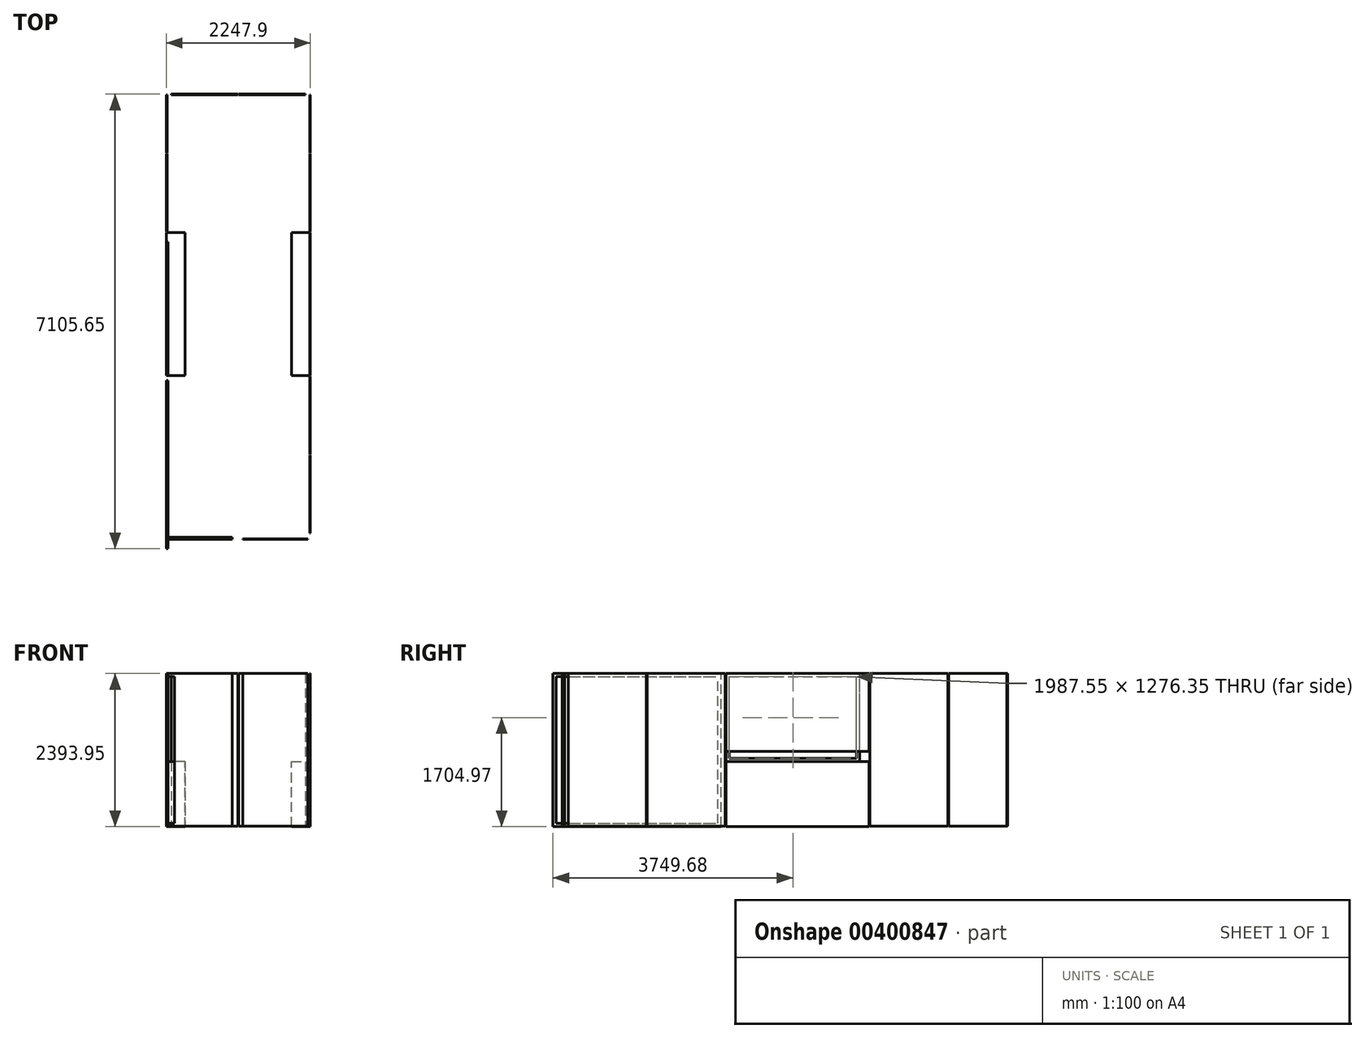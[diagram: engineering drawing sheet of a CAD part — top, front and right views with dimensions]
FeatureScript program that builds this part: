
annotation { "Feature Type Name" : "Feature", "Feature Type Description" : "" }
export const myFeature = defineFeature(function(context is Context, id is Id, definition is map)
    precondition{}
    {
        {
            var Q0;
            Q0=qCreatedBy(makeId("Top.planeOp"),FACE);
            var sketch = newSketch(context, id + "F0", { "sketchPlane" : qUnion([Q0])});
            skLineSegment(sketch, "E0.bottom", {"start": v(0, -6959.6) * mm, "end": v(2247.9, -6959.6) * mm});
            skLineSegment(sketch, "E0.top", {"start": v(0, 0) * mm, "end": v(2247.9, 0) * mm});
            skLineSegment(sketch, "E0.left", {"start": v(0, -6959.6) * mm, "end": v(0, 0) * mm});
            skLineSegment(sketch, "E0.right", {"start": v(2247.9, -6959.6) * mm, "end": v(2247.9, 0) * mm});
            skSolve(sketch);
        }
        {
            var Q0;
            Q0=qSketchRegion(id+"F0",true);
            extrude(context, id + "F1", {"entities" : qUnion([Q0]), "depth" : 2565.4 * mm});
        }
        {
            var Q0;
            Q0=makeQuery(id+"F1.opExtrude","SWEPT_FACE",FACE,{"disambiguationData":[OSD([sQuery(id+"F0.wireOp",EDGE,"E0.left")])]});
            cPlane(context, id + "F2", {"entities" : qUnion([Q0]), "cplaneType" : CPlaneType.OFFSET, "offset" : 0 * mm, "width" : 152.4 * mm, "height" : 152.4 * mm});
        }
        {
            var Q0;
            Q0=makeQuery(id+"F1.opExtrude","SWEPT_FACE",FACE,{"disambiguationData":[OSD([sQuery(id+"F0.wireOp",EDGE,"E0.right")])]});
            cPlane(context, id + "F3", {"entities" : qUnion([Q0]), "cplaneType" : CPlaneType.OFFSET, "offset" : 0 * mm, "width" : 152.4 * mm, "height" : 152.4 * mm});
        }
        {
            var Q0;
            Q0=makeQuery(id+"F1.opExtrude","SWEPT_FACE",FACE,{"disambiguationData":[OSD([sQuery(id+"F0.wireOp",EDGE,"E0.top")])]});
            cPlane(context, id + "F4", {"entities" : qUnion([Q0]), "cplaneType" : CPlaneType.OFFSET, "offset" : 0 * mm, "width" : 152.4 * mm, "height" : 152.4 * mm});
        }
        {
            var Q0;
            Q0=makeQuery(id+"F1.opExtrude","SWEPT_FACE",FACE,{"disambiguationData":[OSD([sQuery(id+"F0.wireOp",EDGE,"E0.bottom")])]});
            cPlane(context, id + "F5", {"entities" : qUnion([Q0]), "cplaneType" : CPlaneType.OFFSET, "offset" : 0 * mm, "width" : 152.4 * mm, "height" : 152.4 * mm});
        }
        {
            var Q0;
            Q0=qCreatedBy(id+"F3.planeOp",FACE);
            var sketch = newSketch(context, id + "F6", { "sketchPlane" : qUnion([Q0])});
            skLineSegment(sketch, "E1.bottom", {"start": v(-5632.45, 6.35) * mm, "end": v(-4413.25, 6.35) * mm});
            skLineSegment(sketch, "E1.top", {"start": v(-5632.45, 2393.95) * mm, "end": v(-4413.25, 2393.95) * mm});
            skLineSegment(sketch, "E1.left", {"start": v(-5632.45, 6.35) * mm, "end": v(-5632.45, 2393.95) * mm});
            skLineSegment(sketch, "E1.right", {"start": v(-4413.25, 6.35) * mm, "end": v(-4413.25, 2393.95) * mm});
            skLineSegment(sketch, "E2.bottom", {"start": v(-4400.55, 2393.95) * mm, "end": v(-2165.35, 2393.95) * mm});
            skLineSegment(sketch, "E2.top", {"start": v(-4400.55, 1174.75) * mm, "end": v(-2165.35, 1174.75) * mm});
            skLineSegment(sketch, "E2.left", {"start": v(-4400.55, 2393.95) * mm, "end": v(-4400.55, 1174.75) * mm});
            skLineSegment(sketch, "E2.right", {"start": v(-2165.35, 2393.95) * mm, "end": v(-2165.35, 1174.75) * mm});
            skLineSegment(sketch, "E3.bottom", {"start": v(-2152.65, 2393.95) * mm, "end": v(-933.45, 2393.95) * mm});
            skLineSegment(sketch, "E3.top", {"start": v(-2152.65, 6.35) * mm, "end": v(-933.45, 6.35) * mm});
            skLineSegment(sketch, "E3.left", {"start": v(-2152.65, 2393.95) * mm, "end": v(-2152.65, 6.35) * mm});
            skLineSegment(sketch, "E3.right", {"start": v(-933.45, 2393.95) * mm, "end": v(-933.45, 6.35) * mm});
            skLineSegment(sketch, "E4.bottom", {"start": v(-6864.35, 6.35) * mm, "end": v(-5645.15, 6.35) * mm});
            skLineSegment(sketch, "E4.top", {"start": v(-6864.35, 2393.95) * mm, "end": v(-5645.15, 2393.95) * mm});
            skLineSegment(sketch, "E4.left", {"start": v(-6864.35, 6.35) * mm, "end": v(-6864.35, 2393.95) * mm});
            skLineSegment(sketch, "E4.right", {"start": v(-5645.15, 6.35) * mm, "end": v(-5645.15, 2393.95) * mm});
            skLineSegment(sketch, "E5.bottom", {"start": v(-2165.35, 0) * mm, "end": v(-4400.55, 0) * mm});
            skLineSegment(sketch, "E5.top", {"start": v(-2165.35, 1016) * mm, "end": v(-4400.55, 1016) * mm});
            skLineSegment(sketch, "E5.left", {"start": v(-2165.35, 0) * mm, "end": v(-2165.35, 1016) * mm});
            skLineSegment(sketch, "E5.right", {"start": v(-4400.55, 0) * mm, "end": v(-4400.55, 1016) * mm});
            skLineSegment(sketch, "E6.bottom", {"start": v(-920.75, 2393.95) * mm, "end": v(-12.7, 2393.95) * mm});
            skLineSegment(sketch, "E6.top", {"start": v(-920.75, 6.35) * mm, "end": v(-12.7, 6.35) * mm});
            skLineSegment(sketch, "E6.left", {"start": v(-920.75, 2393.95) * mm, "end": v(-920.75, 6.35) * mm});
            skLineSegment(sketch, "E6.right", {"start": v(-12.7, 2393.95) * mm, "end": v(-12.7, 6.35) * mm});
            skSolve(sketch);
        }
        {
            var Q0;
            Q0=makeQuery(id+"F6.imprint","IMPRINT",FACE,{"disambiguationData":[TD([[makeQuery(id+"F6.imprint","IMPRINT",EDGE,{"derivedFrom":sQuery(id+"F6.wireOp",EDGE,"E1.bottom")}),1.0]])]});
            var Q1;
            Q1=makeQuery(id+"F6.imprint","IMPRINT",FACE,{"disambiguationData":[TD([[makeQuery(id+"F6.imprint","IMPRINT",EDGE,{"derivedFrom":sQuery(id+"F6.wireOp",EDGE,"E2.bottom")}),-1.0]])]});
            var Q2;
            Q2=makeQuery(id+"F6.imprint","IMPRINT",FACE,{"disambiguationData":[TD([[makeQuery(id+"F6.imprint","IMPRINT",EDGE,{"derivedFrom":sQuery(id+"F6.wireOp",EDGE,"E3.bottom")}),-1.0]])]});
            var Q3;
            Q3=makeQuery(id+"F6.imprint","IMPRINT",FACE,{"disambiguationData":[TD([[makeQuery(id+"F6.imprint","IMPRINT",EDGE,{"derivedFrom":sQuery(id+"F6.wireOp",EDGE,"E4.bottom")}),1.0]])]});
            var Q4;
            Q4=makeQuery(id+"F6.imprint","IMPRINT",FACE,{"disambiguationData":[TD([[makeQuery(id+"F6.imprint","IMPRINT",EDGE,{"derivedFrom":sQuery(id+"F6.wireOp",EDGE,"E6.bottom")}),-1.0]])]});
            extrude(context, id + "F7", {"entities" : qUnion([Q0, Q1, Q2, Q3, Q4]), "oppositeDirection" : true, "depth" : 9.52 * mm});
        }
        {
            var Q0;
            Q0=qCreatedBy(id+"F2.planeOp",FACE);
            var sketch = newSketch(context, id + "F8", { "sketchPlane" : qUnion([Q0])});
            skLineSegment(sketch, "E7.bottom", {"start": v(7105.65, 0) * mm, "end": v(4476.75, 0) * mm});
            skLineSegment(sketch, "E7.top", {"start": v(7105.65, 2393.95) * mm, "end": v(4476.75, 2393.95) * mm});
            skLineSegment(sketch, "E7.left", {"start": v(7105.65, 0) * mm, "end": v(7105.65, 2393.95) * mm});
            skLineSegment(sketch, "E7.right", {"start": v(4476.75, 0) * mm, "end": v(4476.75, 2393.95) * mm});
            skLineSegment(sketch, "E8.bottom", {"start": v(2152.65, 2393.95) * mm, "end": v(933.45, 2393.95) * mm});
            skLineSegment(sketch, "E8.top", {"start": v(2152.65, 6.35) * mm, "end": v(933.45, 6.35) * mm});
            skLineSegment(sketch, "E8.left", {"start": v(2152.65, 2393.95) * mm, "end": v(2152.65, 6.35) * mm});
            skLineSegment(sketch, "E8.right", {"start": v(933.45, 2393.95) * mm, "end": v(933.45, 6.35) * mm});
            skLineSegment(sketch, "E9.bottom", {"start": v(4400.55, 1016) * mm, "end": v(2311.4, 1016) * mm});
            skLineSegment(sketch, "E9.top", {"start": v(4400.55, 2393.95) * mm, "end": v(2311.4, 2393.95) * mm});
            skLineSegment(sketch, "E9.left", {"start": v(4400.55, 1016) * mm, "end": v(4400.55, 2393.95) * mm});
            skLineSegment(sketch, "E9.right", {"start": v(2311.4, 1016) * mm, "end": v(2311.4, 2393.95) * mm});
            skLineSegment(sketch, "E10.0.0", {"start": v(2165.35, 0) * mm, "end": v(2165.35, 1016) * mm});
            skLineSegment(sketch, "E10.0.1", {"start": v(2165.35, 1016) * mm, "end": v(4400.55, 1016) * mm});
            skLineSegment(sketch, "E10.0.2", {"start": v(4400.55, 1016) * mm, "end": v(4400.55, 0) * mm});
            skLineSegment(sketch, "E10.0.3", {"start": v(4400.55, 0) * mm, "end": v(2165.35, 0) * mm});
            skLineSegment(sketch, "E11.bottom", {"start": v(920.75, 2393.95) * mm, "end": v(12.7, 2393.95) * mm});
            skLineSegment(sketch, "E11.top", {"start": v(920.75, 6.35) * mm, "end": v(12.7, 6.35) * mm});
            skLineSegment(sketch, "E11.left", {"start": v(920.75, 2393.95) * mm, "end": v(920.75, 6.35) * mm});
            skLineSegment(sketch, "E11.right", {"start": v(12.7, 2393.95) * mm, "end": v(12.7, 6.35) * mm});
            skSolve(sketch);
        }
        {
            var Q0;
            Q0=qCreatedBy(id+"F4.planeOp",FACE);
            var sketch = newSketch(context, id + "F9", { "sketchPlane" : qUnion([Q0])});
            skLineSegment(sketch, "E12.bottom", {"start": v(-1117.6, 2393.95) * mm, "end": v(-76.2, 2393.95) * mm});
            skLineSegment(sketch, "E12.top", {"start": v(-1117.6, 6.35) * mm, "end": v(-76.2, 6.35) * mm});
            skLineSegment(sketch, "E12.left", {"start": v(-1117.6, 2393.95) * mm, "end": v(-1117.6, 6.35) * mm});
            skLineSegment(sketch, "E12.right", {"start": v(-76.2, 2393.95) * mm, "end": v(-76.2, 6.35) * mm});
            skLineSegment(sketch, "E13.bottom", {"start": v(-1130.3, 2393.95) * mm, "end": v(-2171.7, 2393.95) * mm});
            skLineSegment(sketch, "E13.top", {"start": v(-1130.3, 6.35) * mm, "end": v(-2171.7, 6.35) * mm});
            skLineSegment(sketch, "E13.left", {"start": v(-1130.3, 2393.95) * mm, "end": v(-1130.3, 6.35) * mm});
            skLineSegment(sketch, "E13.right", {"start": v(-2171.7, 2393.95) * mm, "end": v(-2171.7, 6.35) * mm});
            skSolve(sketch);
        }
        {
            var Q0;
            Q0=makeQuery(id+"F6.imprint","IMPRINT",FACE,{"disambiguationData":[TD([[makeQuery(id+"F6.imprint","IMPRINT",EDGE,{"derivedFrom":sQuery(id+"F6.wireOp",EDGE,"E5.bottom")}),-1.0]])]});
            extrude(context, id + "F10", {"entities" : qUnion([Q0]), "oppositeDirection" : true, "depth" : 292.1 * mm});
        }
        {
            var Q0;
            Q0=qCreatedBy(id+"F5.planeOp",FACE);
            var sketch = newSketch(context, id + "F11", { "sketchPlane" : qUnion([Q0])});
            skLineSegment(sketch, "E14.bottom", {"start": v(2209.8, 6.35) * mm, "end": v(1193.8, 6.35) * mm});
            skLineSegment(sketch, "E14.top", {"start": v(2209.8, 2393.95) * mm, "end": v(1193.8, 2393.95) * mm});
            skLineSegment(sketch, "E14.left", {"start": v(2209.8, 6.35) * mm, "end": v(2209.8, 2393.95) * mm});
            skLineSegment(sketch, "E14.right", {"start": v(1193.8, 6.35) * mm, "end": v(1193.8, 2393.95) * mm});
            skLineSegment(sketch, "E15.bottom", {"start": v(1028.7, 2393.95) * mm, "end": v(12.7, 2393.95) * mm});
            skLineSegment(sketch, "E15.top", {"start": v(1028.7, 6.35) * mm, "end": v(-12.7, 6.35) * mm});
            skLineSegment(sketch, "E15.left", {"start": v(1028.7, 2393.95) * mm, "end": v(1028.7, 6.35) * mm});
            skLineSegment(sketch, "E15.right", {"start": v(12.7, 2393.95) * mm, "end": v(12.7, 4.17) * mm});
            skSolve(sketch);
        }
        {
            var Q0;
            Q0=makeQuery(id+"F8.imprint","IMPRINT",FACE,{"disambiguationData":[TD([[makeQuery(id+"F8.imprint","IMPRINT",EDGE,{"derivedFrom":sQuery(id+"F8.wireOp",EDGE,"E7.bottom")}),-1.0]])]});
            var Q1;
            Q1=makeQuery(id+"F8.imprint","IMPRINT",FACE,{"disambiguationData":[TD([[makeQuery(id+"F8.imprint","IMPRINT",EDGE,{"derivedFrom":sQuery(id+"F8.wireOp",EDGE,"E9.top")}),1.0]])]});
            extrude(context, id + "F12", {"entities" : qUnion([Q0, Q1]), "oppositeDirection" : true, "depth" : 25.4 * mm});
        }
        {
            var Q0;
            {var subQ3=sQuery(id+"F8.wireOp",EDGE,"E10.0.0");Q0=makeQuery(id+"F8.imprint","IMPRINT",FACE,{"disambiguationData":[TD([[makeQuery(id+"F8.imprint","IMPRINT",EDGE,{"derivedFrom":subQ3}),-1.0]])]});}
            extrude(context, id + "F13", {"entities" : qUnion([Q0]), "oppositeDirection" : true, "depth" : 292.1 * mm});
        }
        {
            var Q0;
            Q0=makeQuery(id+"F8.imprint","IMPRINT",FACE,{"disambiguationData":[TD([[makeQuery(id+"F8.imprint","IMPRINT",EDGE,{"derivedFrom":sQuery(id+"F8.wireOp",EDGE,"E8.bottom")}),1.0]])]});
            var Q1;
            Q1=makeQuery(id+"F8.imprint","IMPRINT",FACE,{"disambiguationData":[TD([[makeQuery(id+"F8.imprint","IMPRINT",EDGE,{"derivedFrom":sQuery(id+"F8.wireOp",EDGE,"E11.bottom")}),1.0]])]});
            extrude(context, id + "F14", {"entities" : qUnion([Q0, Q1]), "oppositeDirection" : true, "depth" : 9.52 * mm});
        }
        {
            var Q0;
            Q0=makeQuery(id+"F9.imprint","IMPRINT",FACE,{"disambiguationData":[TD([[makeQuery(id+"F9.imprint","IMPRINT",EDGE,{"derivedFrom":sQuery(id+"F9.wireOp",EDGE,"E12.bottom")}),-1.0]])]});
            var Q1;
            Q1=makeQuery(id+"F9.imprint","IMPRINT",FACE,{"disambiguationData":[TD([[makeQuery(id+"F9.imprint","IMPRINT",EDGE,{"derivedFrom":sQuery(id+"F9.wireOp",EDGE,"E13.bottom")}),1.0]])]});
            extrude(context, id + "F15", {"entities" : qUnion([Q0, Q1]), "oppositeDirection" : true, "depth" : 9.52 * mm});
        }
        {
            var Q0;
            {var subQ0=sQuery(id+"F11.wireOp",EDGE,"E15.bottom");Q0=makeQuery(id+"F11.imprint","IMPRINT",FACE,{"disambiguationData":[TD([[makeQuery(id+"F11.imprint","IMPRINT",EDGE,{"derivedFrom":subQ0}),1.0]])]});}
            var Q1;
            Q1=makeQuery(id+"F11.imprint","IMPRINT",FACE,{"disambiguationData":[TD([[makeQuery(id+"F11.imprint","IMPRINT",EDGE,{"derivedFrom":sQuery(id+"F11.wireOp",EDGE,"E14.bottom")}),-1.0]])]});
            extrude(context, id + "F16", {"entities" : qUnion([Q0, Q1]), "oppositeDirection" : true, "depth" : 9.52 * mm});
        }
        {
            var Q0;
            Q0=makeQuery(id+"F1.opExtrude","SWEPT_BODY",BODY,{"disambiguationData":[OSD([sQuery(id+"F0.wireOp",EDGE,"E0.bottom"),sQuery(id+"F0.wireOp",EDGE,"E0.top"),sQuery(id+"F0.wireOp",EDGE,"E0.left"),sQuery(id+"F0.wireOp",EDGE,"E0.right")])]});
            deleteBodies(context, id + "F17", {"entities" : qUnion([Q0])});
        }
        {
            var Q0;
            Q0=makeQuery(id+"F16.opExtrude","CAP_FACE",FACE,{"disambiguationData":[OSD([sQuery(id+"F11.wireOp",EDGE,"E15.bottom"),sQuery(id+"F11.wireOp",EDGE,"E15.top"),sQuery(id+"F11.wireOp",EDGE,"E15.left"),sQuery(id+"F11.wireOp",EDGE,"E15.right")])],"isStart":false});
            extrude(context, id + "F18", {"entities" : qUnion([Q0]), "operationType" : NewBodyOperationType.ADD, "depth" : 25.4 * mm, "offsetDistance" : 25.4 * mm});
        }
        {
            var Q0;
            Q0=makeQuery(id+"F8.imprint","IMPRINT",FACE,{"disambiguationData":[TD([[makeQuery(id+"F8.imprint","IMPRINT",EDGE,{"derivedFrom":sQuery(id+"F8.wireOp",EDGE,"E7.bottom")}),-1.0]])]});
            var sketch = newSketch(context, id + "F19", { "sketchPlane" : qUnion([Q0])});
            skLineSegment(sketch, "E16.0", {"start": v(7105.65, 2393.95) * mm, "end": v(4476.75, 2393.95) * mm, "construction": true});
            skLineSegment(sketch, "E16.1", {"start": v(4476.75, 0) * mm, "end": v(4476.75, 2393.95) * mm, "construction": true});
            skLineSegment(sketch, "E16.2", {"start": v(7105.65, 0) * mm, "end": v(4476.75, 0) * mm});
            skLineSegment(sketch, "E16.3", {"start": v(7105.65, 0) * mm, "end": v(7105.65, 2393.95) * mm, "construction": true});
            skLineSegment(sketch, "E17.0", {"start": v(7054.85, 2343.15) * mm, "end": v(4527.55, 2343.15) * mm});
            skLineSegment(sketch, "E17.1", {"start": v(7054.85, 50.8) * mm, "end": v(7054.85, 2343.15) * mm});
            skLineSegment(sketch, "E17.2", {"start": v(7054.85, 50.8) * mm, "end": v(4527.55, 50.8) * mm});
            skLineSegment(sketch, "E17.3", {"start": v(4527.55, 50.8) * mm, "end": v(4527.55, 2343.15) * mm});
            skSolve(sketch);
        }
        {
            var Q0;
            Q0 = qSketchRegion(id + "F19", true);
            extrude(context, id + "F20", {"entities" : qUnion([Q0]), "operationType" : NewBodyOperationType.REMOVE, "oppositeDirection" : true, "depth" : 127 * mm, "offsetDistance" : 25.4 * mm});
        }
        {
            var Q0;
            Q0=makeQuery(id+"F8.imprint","IMPRINT",FACE,{"disambiguationData":[TD([[makeQuery(id+"F8.imprint","IMPRINT",EDGE,{"derivedFrom":sQuery(id+"F8.wireOp",EDGE,"E9.top")}),1.0]])]});
            var sketch = newSketch(context, id + "F21", { "sketchPlane" : qUnion([Q0])});
            skLineSegment(sketch, "E18.0", {"start": v(2165.35, 1016) * mm, "end": v(4400.55, 1016) * mm});
            skLineSegment(sketch, "E18.1", {"start": v(2311.4, 1016) * mm, "end": v(2311.4, 2393.95) * mm, "construction": true});
            skLineSegment(sketch, "E18.2", {"start": v(2152.65, 2393.95) * mm, "end": v(933.45, 2393.95) * mm});
            skLineSegment(sketch, "E19.0", {"start": v(2311.4, 1016) * mm, "end": v(4400.55, 1016) * mm, "construction": true});
            skLineSegment(sketch, "E19.3", {"start": v(4400.55, 2393.95) * mm, "end": v(2165.35, 2393.95) * mm, "construction": true});
            skLineSegment(sketch, "E19.4", {"start": v(4400.55, 1016) * mm, "end": v(4400.55, 2393.95) * mm, "construction": true});
            skLineSegment(sketch, "E20.0", {"start": v(4349.75, 1066.8) * mm, "end": v(4349.75, 2343.15) * mm});
            skLineSegment(sketch, "E20.1", {"start": v(2362.2, 1066.8) * mm, "end": v(4349.75, 1066.8) * mm});
            skLineSegment(sketch, "E20.2", {"start": v(2362.2, 1066.8) * mm, "end": v(2362.2, 2343.15) * mm});
            skLineSegment(sketch, "E20.3", {"start": v(4349.75, 2343.15) * mm, "end": v(2362.2, 2343.15) * mm});
            skSolve(sketch);
        }
        {
            var Q0;
            Q0=makeQuery(id+"F21.imprint","IMPRINT",FACE,{"disambiguationData":[TD([[makeQuery(id+"F21.imprint","IMPRINT",EDGE,{"derivedFrom":sQuery(id+"F21.wireOp",EDGE,"E20.0")}),1.0]])]});
            var Q1;
            Q1=sQuery(id+"F21.wireOp",EDGE,"E20.3");
            var Q2;
            Q2=sQuery(id+"F21.wireOp",EDGE,"E20.0");
            var Q3;
            Q3=sQuery(id+"F21.wireOp",EDGE,"E20.1");
            var Q4;
            Q4=sQuery(id+"F21.wireOp",EDGE,"E20.2");
            extrude(context, id + "F22", {"entities" : qUnion([Q0]), "operationType" : NewBodyOperationType.REMOVE, "surfaceEntities" : qUnion([Q1, Q2, Q3, Q4]), "oppositeDirection" : true, "depth" : 127 * mm, "offsetDistance" : 25.4 * mm});
        }
    });
